# Revit family: Wall_Hung _Multiple_Station_Hand_Wash_Sink_Kit-Elkay-EWMA9620C
name_source: partatom
category: Plumbing Fixtures
units: mm (PartAtom-declared; Revit-internal decimal feet)

## family parameters
Cut with Voids When Loaded = No
Host = Face
Maintain Annotation Orientation = No
OmniClass Number = 23.45.05.14.14
OmniClass Title = Sinks/Lavatories
Part Type = Normal
Room Calculation Point = No
Round Connector Dimension = Use Diameter
Shared = No

## types (1)
- EWMA9620C (Wall Hung Multiple Station Wash Sink Kit)
    Approx. Shipping Weight (lbs) = 149
    Assembly Code = D2010400
    Back splash Height = 10.00"
    Back splash width = 2.00"
    Bowl  Dimensions = 93 inch x 16 1/2 inch x 8 inch
    Bowl Width = 16.50"
    Bowl length = 93.00"
    C/C distance of holes = 16.00"
    CL of Hole = 3.50"
    CWFU = 1
    Default Elevation = 48.00"
    Description = Stainless Steel 96 inch x 20 inch x 18 inch Wall Hung Multiple Station Hand Wash Sink Kit w/Faucets + Drain
    Distance b/w 2 Holes = 16.00"
    Drain Location = Center
    Drain Location along x-axis = 46.50"
    Drain Location along y-axis = 6.88"
    Drain Size = 3 1/2
    Front rim = 1.50"
    Guage = 14
    HWFU = 1
    Inlet Connection Size (inch) = 0.50"
    Installation type = Wall Hung
    Main Material = Finish-Elkay-Stainless Steel
    Manufacturer = Elkay Manufacturer Company
    Manufacturer Brand = Elkay (by Zurn Elkay Water Solutions)
    Model = EWMA9620C
    No of Bowls = 1
    Outlet Connection Size (inch) = 1.50"
    Product Documentation Link = https://www.elkayfiles.com
    Product Installation Sheet URL = https://www.elkayfiles.com
    Product Page URL = https://www.elkay.com
    Product Weight (lbs) = 138
    Product data URL = https://www.bimobject.com
    Repair Parts URL = https://www.elkayfiles.com
    Rim = 1.50"
    Sink Depth = 18.00"
    Sink Dimensions = 96 inch x 20 inch x 18 inch
    Sink Length = 96.00"
    Sink Width = 20.00"
    URL = https://www.elkay.com

## geometry (parser evidence)
native form markers: Blend x2, Sweep x8
no freeform markers — native parametric forms only
